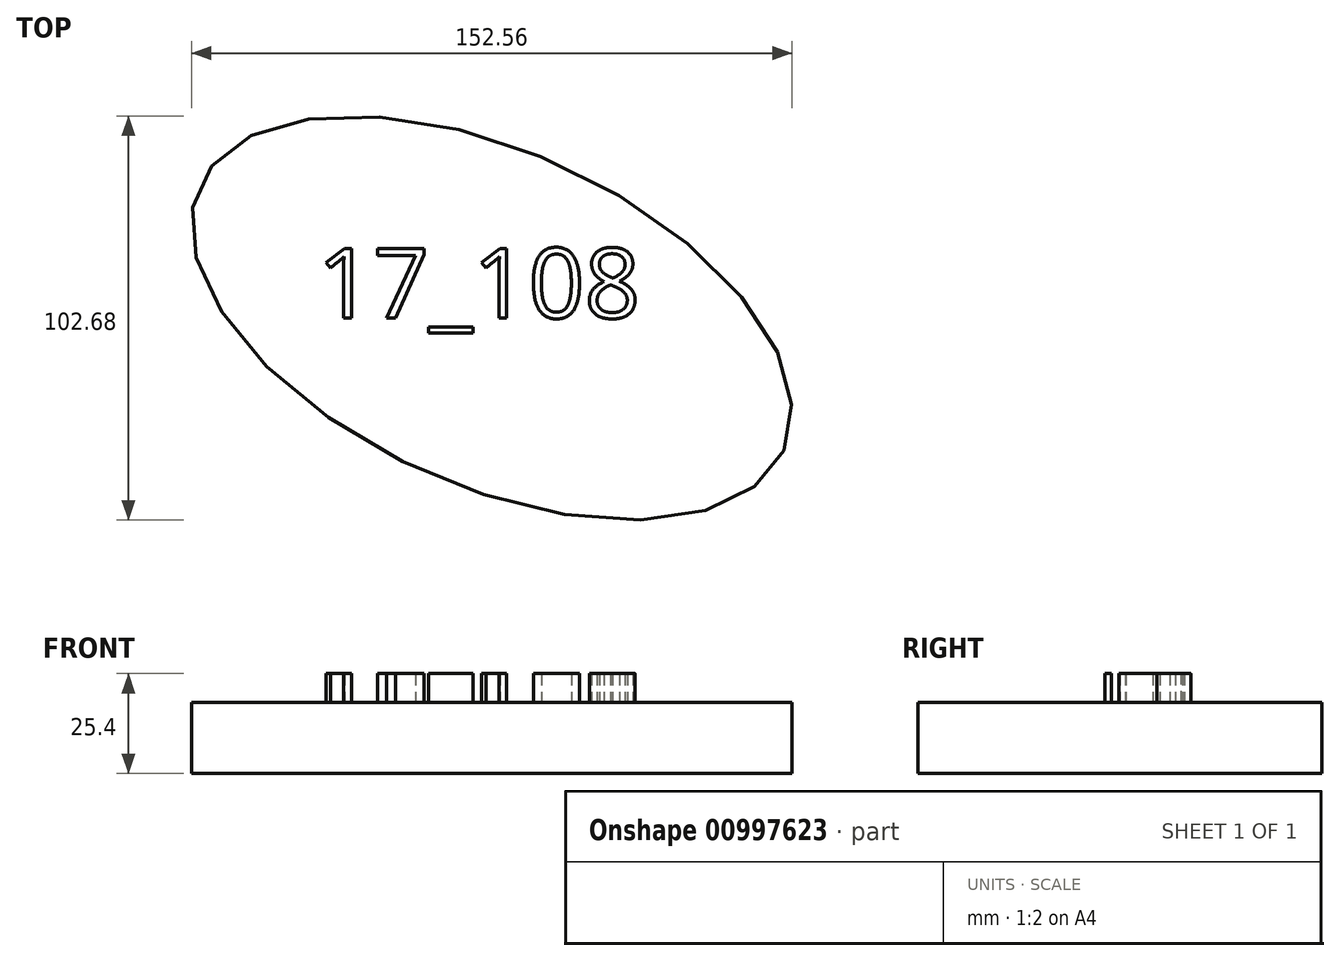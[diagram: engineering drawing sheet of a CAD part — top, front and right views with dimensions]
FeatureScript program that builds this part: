
annotation { "Feature Type Name" : "Feature", "Feature Type Description" : "" }
export const myFeature = defineFeature(function(context is Context, id is Id, definition is map)
    precondition{}
    {
        {
            var Q0;
            Q0=qCreatedBy(makeId("Top.planeOp"),FACE);
            var sketch = newSketch(context, id + "F0", { "sketchPlane" : qUnion([Q0])});
            skEllipse(sketch, "E0", {"center": v(0, 0) * mm, "majorRadius": 81.5 * mm, "minorRadius": 42.59 * mm, "majorAxis": v(0.91, -0.41)});
            skSolve(sketch);
        }
        {
            var Q0;
            Q0=makeQuery(id+"F0.imprint","IMPRINT",FACE,{"disambiguationData":[TD([[makeQuery(id+"F0.imprint","IMPRINT",EDGE,{"derivedFrom":sQuery(id+"F0.wireOp",EDGE,"E0")}),1.0]])]});
            extrude(context, id + "F1", {"entities" : qUnion([Q0]), "depth" : 18.03 * mm, "offsetDistance" : 25.4 * mm});
        }
        {
            var Q0;
            Q0=qCreatedBy(makeId("Top.planeOp"),FACE);
            var sketch = newSketch(context, id + "F2", { "sketchPlane" : qUnion([Q0])});
            skText(sketch, "E1", { "text": "17_108", "fontName": "OpenSans-Regular.ttf"});
            const initialGuessF2  = {"E1": [-0.0443, 0, 1, 0, 0.01786]};
            skSetInitialGuess(sketch, initialGuessF2);
            skSolve(sketch);
        }
        {
            var Q0;
            Q0 = qSketchRegion(id + "F2", true);
            extrude(context, id + "F3", {"entities" : qUnion([Q0]), "operationType" : NewBodyOperationType.ADD, "depth" : 25.4 * mm, "offsetDistance" : 25.4 * mm});
        }
    });
